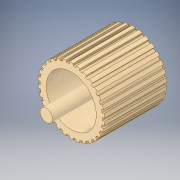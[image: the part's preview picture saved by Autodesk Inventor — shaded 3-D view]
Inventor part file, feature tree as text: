
AUTODESK INVENTOR PART (.ipt)
format: ipt  version: 2018.1 (Build 221171000, 171)  size: 317,952 bytes
history: native  units: mm
features: extrude x3, sketch x3, other x1
ambient origin geometry x8: Origin, YZ Plane, XZ Plane, XY Plane, X Axis, Y Axis, Z Axis, Center Point
bodies: Body1 (feature_tree)
feature tree (7):
  other  "ソリッド1"
  extrude  "押し出し1"  Depth=50.0mm
  extrude  "押し出し2"  Depth=3.0mm
  extrude  "押し出し3"  Depth=3.0mm
  sketch  "スケッチ1"
  sketch  "スケッチ2"
  sketch  "スケッチ3"
